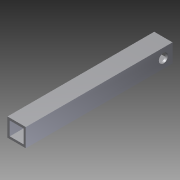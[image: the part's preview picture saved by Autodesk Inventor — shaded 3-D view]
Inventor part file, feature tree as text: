
AUTODESK INVENTOR PART (.ipt)
format: ipt  version: 2012 (Build 160160000, 160)  size: 88,064 bytes
history: native  units: in
note: dims shown in document units (in); Inventor stores cm internally (conversion verified against a paired STEP export)
features: extrude x2, sketch x2
ambient origin geometry x8: Origin, YZ Plane, XZ Plane, XY Plane, X Axis, Y Axis, Z Axis, Center Point
bodies: Solid1 (feature_tree)
feature tree (4):
  extrude  "Extrusion1"  Depth=0.125in
  extrude  "Extrusion2"  Depth=0.125in
  sketch  "Sketch1"  dims[d0=0.125in d1=0.125in]
  sketch  "Sketch2"  dims[d2=0.125in d3=0.125in d4=1.0in d5=1.0in d6=8.0in d7=0.0in d8=0.5in d9=0.5in d10=0.5in d11=8.0in d12=0.0in]
